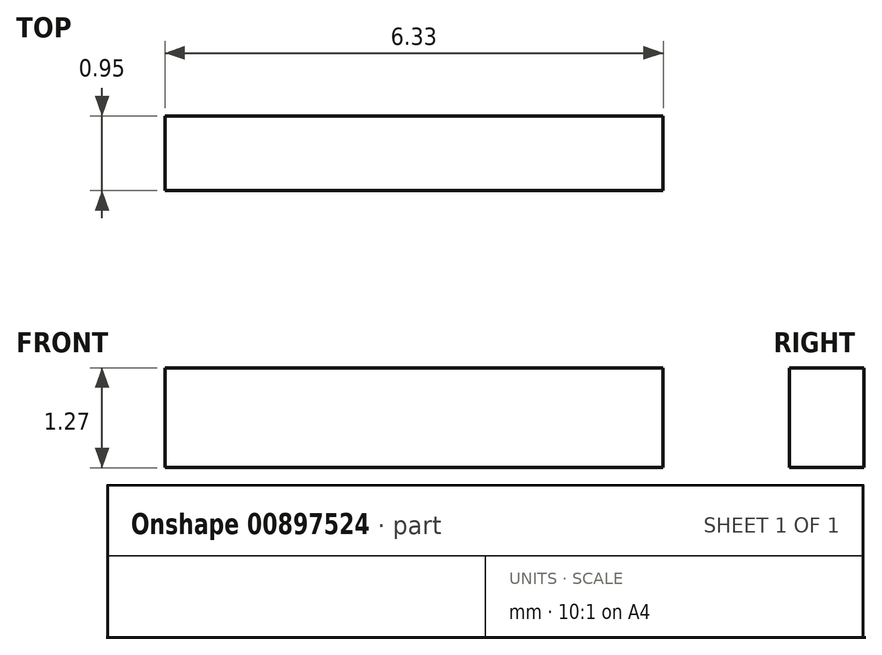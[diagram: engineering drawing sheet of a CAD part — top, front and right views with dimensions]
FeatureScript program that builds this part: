
annotation { "Feature Type Name" : "Feature", "Feature Type Description" : "" }
export const myFeature = defineFeature(function(context is Context, id is Id, definition is map)
    precondition{}
    {
        {
            var Q0;
            Q0=qCreatedBy(makeId("Front.planeOp"),FACE);
            var sketch = newSketch(context, id + "F0", { "sketchPlane" : qUnion([Q0])});
            skLineSegment(sketch, "E0.bottom", {"start": v(-103.61, 7.9) * mm, "end": v(-97.28, 7.9) * mm});
            skLineSegment(sketch, "E0.top", {"start": v(-103.61, 6.63) * mm, "end": v(-97.28, 6.63) * mm});
            skLineSegment(sketch, "E0.left", {"start": v(-103.61, 7.9) * mm, "end": v(-103.61, 6.63) * mm});
            skLineSegment(sketch, "E0.right", {"start": v(-97.28, 7.9) * mm, "end": v(-97.28, 6.63) * mm});
            skSolve(sketch);
        }
        {
            var Q0;
            Q0 = qSketchRegion(id + "F0", true);
            extrude(context, id + "F1", {"entities" : qUnion([Q0]), "depth" : 0.95 * mm, "offsetDistance" : 25 * mm});
        }
    });
